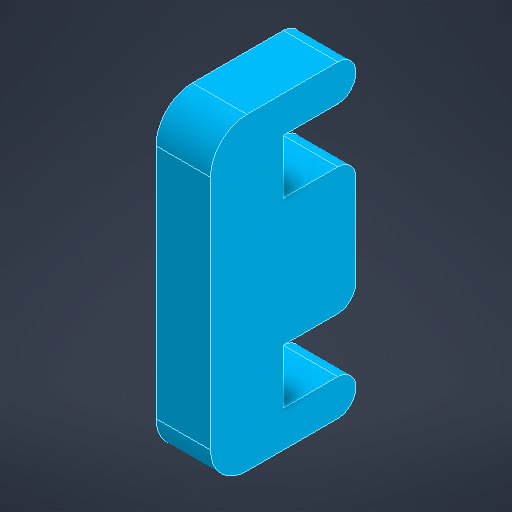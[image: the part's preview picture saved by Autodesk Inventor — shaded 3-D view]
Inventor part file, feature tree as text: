
AUTODESK INVENTOR PART (.ipt)
format: ipt  version: 2025.3 (Build 293356030, 356C)  size: 211,968 bytes
history: native  units: mm
features: fillet x3, other x1, extrude x1, sketch x1
ambient origin geometry x8: Origin, YZ Plane, XZ Plane, XY Plane, X Axis, Y Axis, Z Axis, Center Point
bodies: Body1 (feature_tree)
feature tree (6):
  other  "實體1"
  extrude  "擠出1"  Depth=3.0mm
  fillet  "圓角1"  Radius=7.0mm
  fillet  "圓角2"  Radius=8.0mm
  fillet  "圓角3"  Radius=4.0mm
  sketch  "草圖1"
